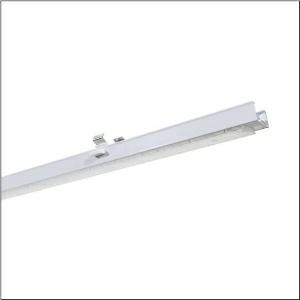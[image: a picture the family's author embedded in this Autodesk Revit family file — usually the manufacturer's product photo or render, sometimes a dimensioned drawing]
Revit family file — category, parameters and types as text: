
# Revit family: trunking_flex_31_51re14mb4cb
name_source: partatom
category: Lighting Fixtures
units: mm (PartAtom-declared; Revit-internal decimal feet)

## family parameters
Cut with Voids When Loaded = No
Host = Face
Light Source = No
Part Type = Normal
Room Calculation Point = No
Round Connector Dimension = Use Diameter
Shared = No

## types (1)
- --- (1 x LED, 11500 lm, 66 W, 4000K)
    Apparent Load = 66 VA
    CIE Flux Codes = 72 92 98 99 100
    Color Rendering = 80
    Color Temperature = 4000K
    Default Elevation = 1800 mm
    Description = Trunking Flex 31, luminaire insert, of extruded aluminium section, coated, traffic white (RAL 9016), length: 1.472mm, width: 91mm, height: 53mm, LED rated luminous flux: 11.500lm, light colour: 840, control gear: ON/OFF Multilumen, with system connector: socket, mains connection: 220..240V, AC, 50/60Hz, rated input power: 66W, connected load according to luminous flux setting (19/24/32/37/47/52/60/66W), luminous flux adjustable on luminaire in eight steps (3450/4380/5800/6700/8350/9200/10500/11500lm ), primary light control with lens, of plastic, primary optical cover: cover, of PMMA, light emission: direct distribution, primary light characteristic: asymmetric, protection rating (complete): IP20, insulation class (complete): insulation class I (protective earthing), certification: CE, UKCA, impact resistance: IK02, permissible ambient temperature for indoor applications: -20..+40°C, packaging unit: 1 piece
    Height = 58 mm
    Lamp = 1 x LED
    Lamp Light Flux = 11500 lm
    Lamp Power = 66 W
    Lamp count = 1
    Length = 1472 mm
    Luminous efficacy = 174 lm/W
    Manufacturer = Siteco
    ModVariant = No
    Model = 51RE14MB4CB
    Mounting Place = Ceiling
    Mounting Type = Pendant
    Number of Poles = 1
    OnlyDefault = Yes
    Power Factor = 1
    Product Name = Trunking Flex 31
    Product group = luminaire insert
    ProductGroupID = 902
    Protection Class = Protection class I
    Protection Degree = IP 20
    RLX_Detail_Level = 1
    RLX_Emergency_Light_Flux = 0 lm
    RLX_Emergency_Type = 0
    RLX_Emergency_Type_DB = No
    RlxData = <blob elided: 21797 chars, md5=03be5881>
    Socket = socket
    Standby Power = 0 W
    System Light Flux = 11500 lm
    System Power = 66 W
    Type Comments = factory setting: luminous flux: 100 % | (ON | ON | ON)
    Type Image = l_1266702.jpg
    URL = http://relux.com
    VarID = @adj_059234
    Voltage = 0 V
    Weight = 0.00 kg
    Width = 65 mm

## geometry (parser evidence)
native form markers: Blend x4, Sweep x10
no freeform markers — native parametric forms only
